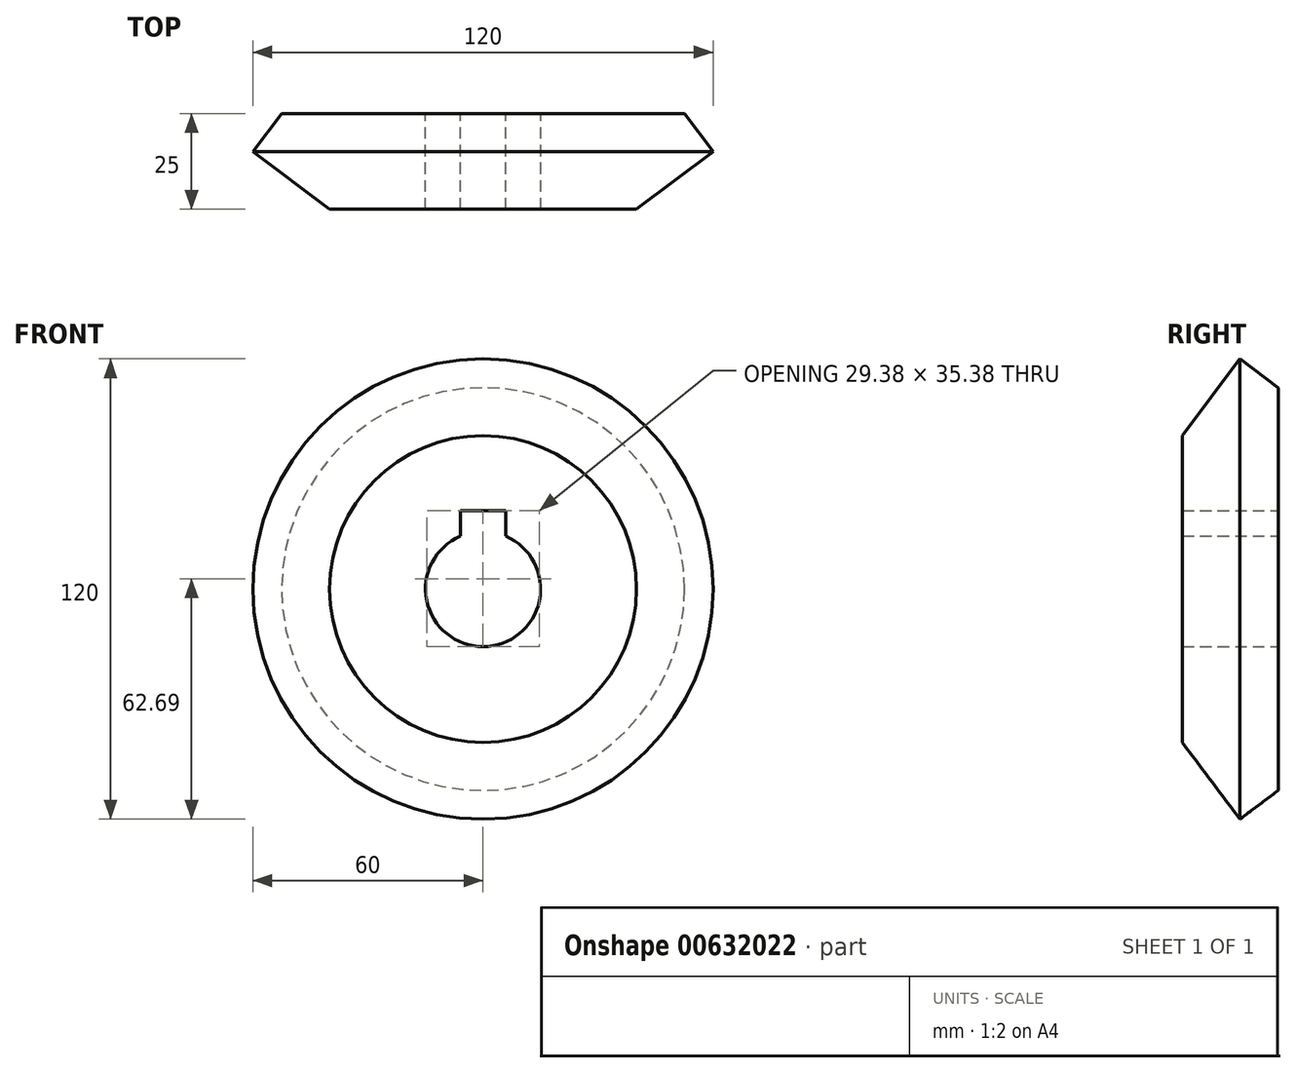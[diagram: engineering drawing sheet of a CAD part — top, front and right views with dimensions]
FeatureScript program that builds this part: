
annotation { "Feature Type Name" : "Feature", "Feature Type Description" : "" }
export const myFeature = defineFeature(function(context is Context, id is Id, definition is map)
    precondition{}
    {
        {
            var Q0;
            Q0=qCreatedBy(makeId("Front.planeOp"),FACE);
            var sketch = newSketch(context, id + "F0", { "sketchPlane" : qUnion([Q0])});
            skCircle(sketch, "E0", {"center": v(0, 0) * mm, "radius": 60 * mm});
            skCircle(sketch, "E1", {"center": v(0, 0) * mm, "radius": 15 * mm});
            skLineSegment(sketch, "E2.bottom", {"start": v(-5.93, 20.38) * mm, "end": v(5.93, 20.38) * mm, "construction": true});
            skLineSegment(sketch, "E2.top", {"start": v(-5.93, -20.38) * mm, "end": v(5.93, -20.38) * mm, "construction": true});
            skLineSegment(sketch, "E2.left", {"start": v(-5.93, 20.38) * mm, "end": v(-5.93, -20.38) * mm, "construction": true});
            skLineSegment(sketch, "E2.right", {"start": v(5.93, 20.38) * mm, "end": v(5.93, -20.38) * mm, "construction": true});
            skLineSegment(sketch, "E3", {"start": v(-5.93, 13.78) * mm, "end": v(5.93, 13.78) * mm, "construction": true});
            skLineSegment(sketch, "E4.bottom", {"start": v(-5.93, 13.78) * mm, "end": v(5.93, 13.78) * mm});
            skLineSegment(sketch, "E4.top", {"start": v(-5.93, 20.38) * mm, "end": v(5.93, 20.38) * mm});
            skLineSegment(sketch, "E4.left", {"start": v(-5.93, 13.78) * mm, "end": v(-5.93, 20.38) * mm});
            skLineSegment(sketch, "E4.right", {"start": v(5.93, 13.78) * mm, "end": v(5.93, 20.38) * mm});
            skSolve(sketch);
        }
        {
            var Q0;
            Q0 = qSketchRegion(id + "F0", true);
            var Q1;
            Q1=makeQuery(id+"F0.imprint","IMPRINT",FACE,{"disambiguationData":[TD([[makeQuery(id+"F0.imprint","IMPRINT",EDGE,{"derivedFrom":sQuery(id+"F0.wireOp",EDGE,"E0")}),1.0]])]});
            extrude(context, id + "F1", {"entities" : qUnion([Q0, Q1]), "depth" : 25 * mm, "offsetDistance" : 25 * mm});
        }
        {
            var Q0;
            Q0=makeQuery(id+"F1.opExtrude","CAP_EDGE",EDGE,{"disambiguationData":[OSD([sQuery(id+"F0.wireOp",EDGE,"E0")])],"isStart":true});
            chamfer(context, id + "F2", {"entities" : qUnion([Q0]), "chamferType" : ChamferType.TWO_OFFSETS, "width1" : 10 * mm, "oppositeDirection" : false, "width2" : 7.5 * mm, "tangentPropagation" : true});
        }
        {
            var Q0;
            Q0=makeQuery(id+"F1.opExtrude","CAP_EDGE",EDGE,{"disambiguationData":[OSD([sQuery(id+"F0.wireOp",EDGE,"E0")])],"isStart":false});
            chamfer(context, id + "F3", {"entities" : qUnion([Q0]), "chamferType" : ChamferType.TWO_OFFSETS, "width1" : 20 * mm, "oppositeDirection" : false, "width2" : 15 * mm, "tangentPropagation" : true});
        }
    });
